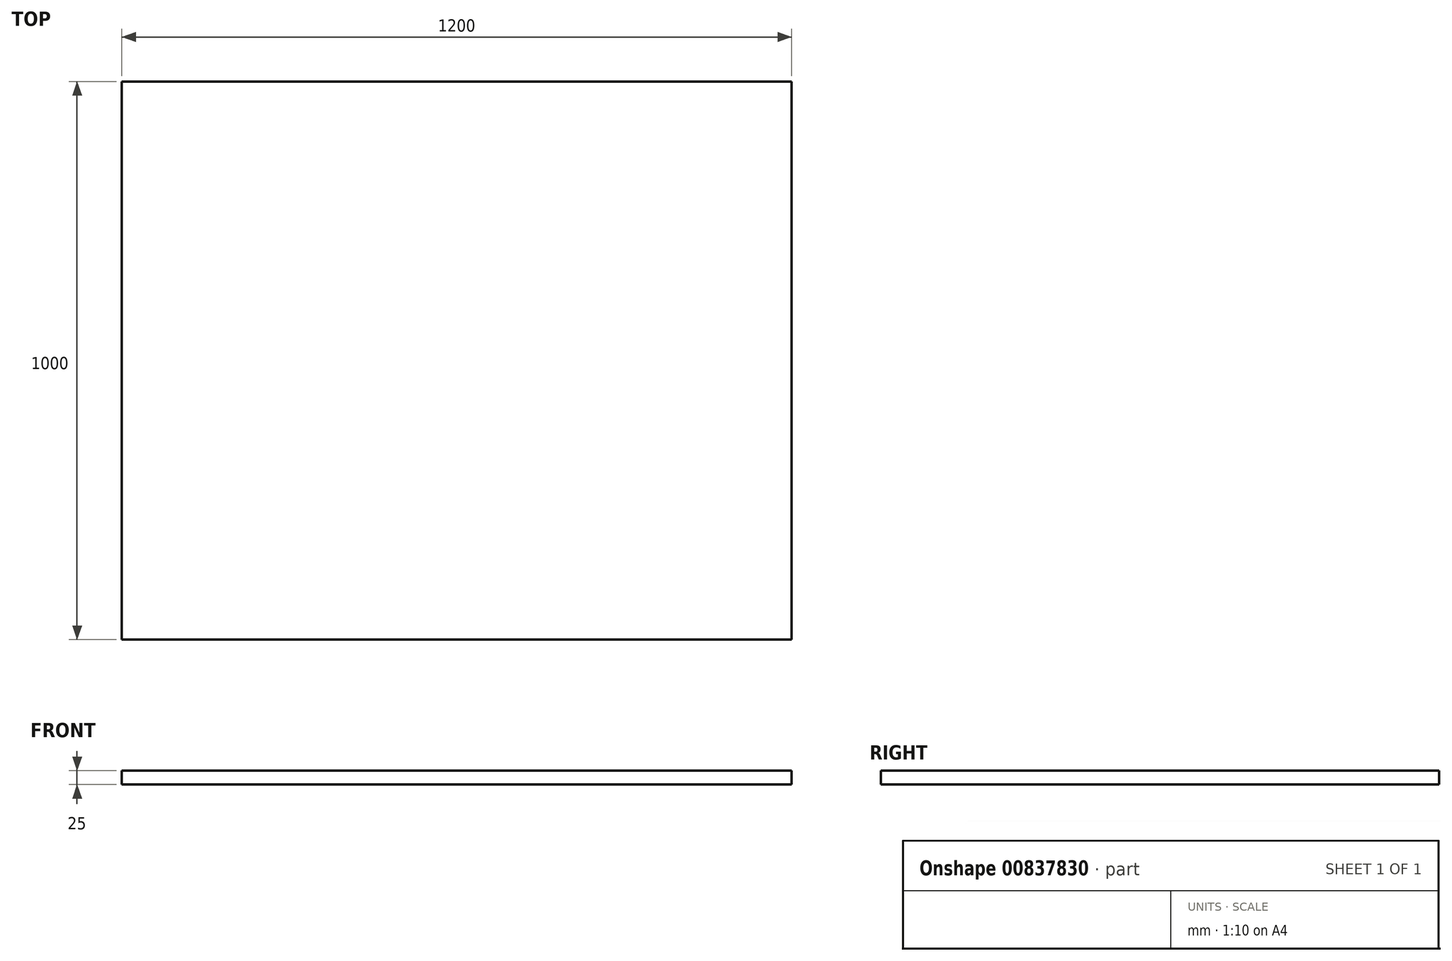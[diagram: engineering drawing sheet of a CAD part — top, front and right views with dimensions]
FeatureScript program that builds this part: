
annotation { "Feature Type Name" : "Feature", "Feature Type Description" : "" }
export const myFeature = defineFeature(function(context is Context, id is Id, definition is map)
    precondition{}
    {
        {
            var Q0;
            Q0=qCreatedBy(makeId("Top.planeOp"),FACE);
            var sketch = newSketch(context, id + "F0", { "sketchPlane" : qUnion([Q0])});
            skLineSegment(sketch, "E0.bottom", {"start": v(600, 500) * mm, "end": v(-600, 500) * mm});
            skLineSegment(sketch, "E0.top", {"start": v(600, -500) * mm, "end": v(-600, -500) * mm});
            skLineSegment(sketch, "E0.left", {"start": v(600, 500) * mm, "end": v(600, -500) * mm});
            skLineSegment(sketch, "E0.right", {"start": v(-600, 500) * mm, "end": v(-600, -500) * mm});
            skPoint(sketch, "E0.middle", {"position": v(0, 0) * mm});
            skSolve(sketch);
        }
        {
            var Q0;
            Q0=makeQuery(id+"F0.imprint","IMPRINT",FACE,{"disambiguationData":[TD([[makeQuery(id+"F0.imprint","IMPRINT",EDGE,{"derivedFrom":sQuery(id+"F0.wireOp",EDGE,"E0.bottom")}),1.0]])]});
            extrude(context, id + "F1", {"entities" : qUnion([Q0]), "depth" : 25 * mm, "offsetDistance" : 25 * mm});
        }
    });
